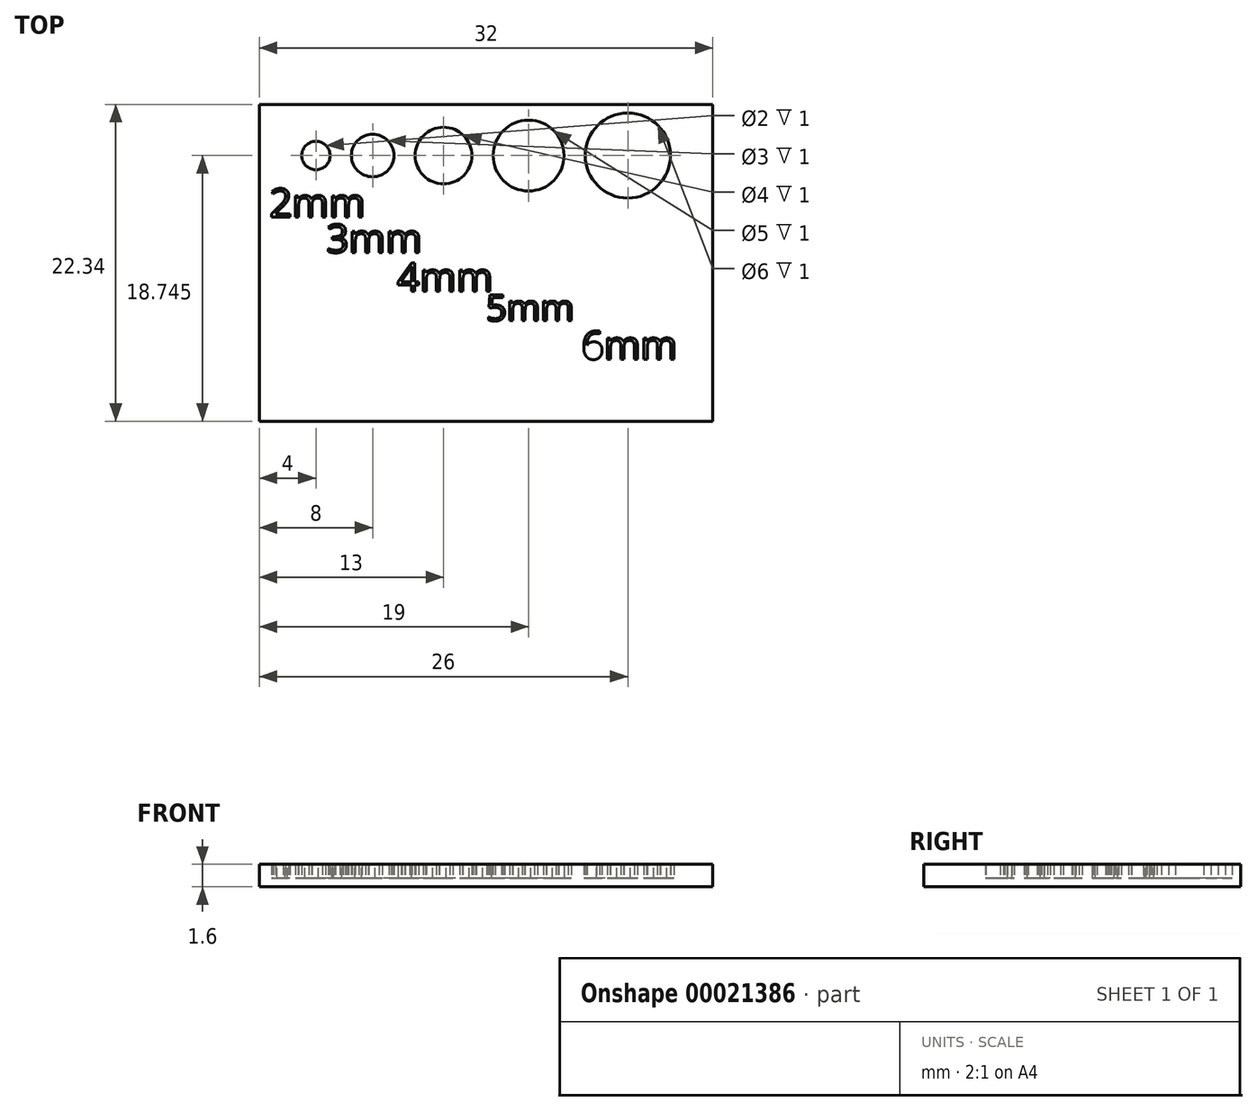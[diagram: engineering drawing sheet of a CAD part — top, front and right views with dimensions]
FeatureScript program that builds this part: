
annotation { "Feature Type Name" : "Feature", "Feature Type Description" : "" }
export const myFeature = defineFeature(function(context is Context, id is Id, definition is map)
    precondition{}
    {
        {
            var Q0;
            Q0=qCreatedBy(makeId("Top.planeOp"),FACE);
            var sketch = newSketch(context, id + "F0", { "sketchPlane" : qUnion([Q0])});
            skLineSegment(sketch, "E0.rect.bottom", {"start": v(-16, 11.17) * mm, "end": v(16, 11.17) * mm});
            skLineSegment(sketch, "E0.rect.top", {"start": v(-16, -11.17) * mm, "end": v(16, -11.17) * mm});
            skLineSegment(sketch, "E0.rect.left", {"start": v(-16, 11.17) * mm, "end": v(-16, -11.17) * mm});
            skLineSegment(sketch, "E0.rect.right", {"start": v(16, 11.17) * mm, "end": v(16, -11.17) * mm});
            skPoint(sketch, "E0.rect.middle", {"position": v(0, 0) * mm});
            skCircle(sketch, "E1", {"center": v(-12, 7.58) * mm, "radius": 1 * mm});
            skCircle(sketch, "E2", {"center": v(-8, 7.58) * mm, "radius": 1.5 * mm});
            skCircle(sketch, "E3", {"center": v(-3, 7.58) * mm, "radius": 2 * mm});
            skCircle(sketch, "E4", {"center": v(3, 7.58) * mm, "radius": 2.5 * mm});
            skCircle(sketch, "E5", {"center": v(10, 7.58) * mm, "radius": 3 * mm});
            skText(sketch, "E6", { "text": "2mm", "fontName": "OpenSans-Regular.ttf"});
            skText(sketch, "E7", { "text": "3mm", "fontName": "OpenSans-Regular.ttf"});
            skText(sketch, "E8", { "text": "4mm", "fontName": "OpenSans-Regular.ttf"});
            skText(sketch, "E9", { "text": "5mm", "fontName": "OpenSans-Regular.ttf"});
            skText(sketch, "E10", { "text": "6mm", "fontName": "OpenSans-Regular.ttf"});
            const initialGuessF0  = {"E6": [-0.01527, 0.00325, 1, 0, 0.002], "E7": [-0.01127, 0.00073, 1, 0, 0.002], "E8": [-0.00627, -0.002, 1, 0, 0.002], "E9": [0, -0.00408, 1, 0, 0.00184], "E10": [0.00673, -0.0068, 1, 0, 0.002]};
            skSetInitialGuess(sketch, initialGuessF0);
            skSolve(sketch);
        }
        {
            var Q0;
            Q0 = qSketchRegion(id + "F0", true);
            var Q1;
            Q1=makeQuery(id+"F0.imprint","IMPRINT",FACE,{"disambiguationData":[TD([[makeQuery(id+"F0.imprint","IMPRINT",EDGE,{"derivedFrom":sQuery(id+"F0.wireOp",EDGE,"E8.sketch_text.stroke-11")}),1.0]])]});
            extrude(context, id + "F1", {"entities" : qUnion([Q0, Q1]), "depth" : 1 * mm});
        }
        {
            var Q0;
            Q0=makeQuery(id+"F1.opExtrude","CAP_FACE",FACE,{"disambiguationData":[OSD([sQuery(id+"F0.wireOp",EDGE,"E0.rect.bottom"),sQuery(id+"F0.wireOp",EDGE,"E0.rect.top"),sQuery(id+"F0.wireOp",EDGE,"E0.rect.left"),sQuery(id+"F0.wireOp",EDGE,"E0.rect.right"),sQuery(id+"F0.wireOp",EDGE,"E1"),sQuery(id+"F0.wireOp",EDGE,"E2"),sQuery(id+"F0.wireOp",EDGE,"E3"),sQuery(id+"F0.wireOp",EDGE,"E4"),sQuery(id+"F0.wireOp",EDGE,"E5"),sQuery(id+"F0.wireOp",EDGE,"E6.sketch_text.stroke-0"),sQuery(id+"F0.wireOp",EDGE,"E6.sketch_text.stroke-1"),sQuery(id+"F0.wireOp",EDGE,"E6.sketch_text.stroke-2"),sQuery(id+"F0.wireOp",EDGE,"E6.sketch_text.stroke-3"),sQuery(id+"F0.wireOp",EDGE,"E6.sketch_text.stroke-4"),sQuery(id+"F0.wireOp",EDGE,"E6.sketch_text.stroke-5"),sQuery(id+"F0.wireOp",EDGE,"E6.sketch_text.stroke-6"),sQuery(id+"F0.wireOp",EDGE,"E6.sketch_text.stroke-7"),sQuery(id+"F0.wireOp",EDGE,"E6.sketch_text.stroke-8"),sQuery(id+"F0.wireOp",EDGE,"E6.sketch_text.stroke-9"),sQuery(id+"F0.wireOp",EDGE,"E6.sketch_text.stroke-10"),sQuery(id+"F0.wireOp",EDGE,"E6.sketch_text.stroke-11"),sQuery(id+"F0.wireOp",EDGE,"E6.sketch_text.stroke-12"),sQuery(id+"F0.wireOp",EDGE,"E6.sketch_text.stroke-13"),sQuery(id+"F0.wireOp",EDGE,"E6.sketch_text.stroke-14"),sQuery(id+"F0.wireOp",EDGE,"E6.sketch_text.stroke-15"),sQuery(id+"F0.wireOp",EDGE,"E6.sketch_text.stroke-16"),sQuery(id+"F0.wireOp",EDGE,"E6.sketch_text.stroke-17"),sQuery(id+"F0.wireOp",EDGE,"E6.sketch_text.stroke-18"),sQuery(id+"F0.wireOp",EDGE,"E6.sketch_text.stroke-19"),sQuery(id+"F0.wireOp",EDGE,"E6.sketch_text.stroke-20"),sQuery(id+"F0.wireOp",EDGE,"E6.sketch_text.stroke-21"),sQuery(id+"F0.wireOp",EDGE,"E6.sketch_text.stroke-22"),sQuery(id+"F0.wireOp",EDGE,"E6.sketch_text.stroke-23"),sQuery(id+"F0.wireOp",EDGE,"E6.sketch_text.stroke-24"),sQuery(id+"F0.wireOp",EDGE,"E6.sketch_text.stroke-25"),sQuery(id+"F0.wireOp",EDGE,"E6.sketch_text.stroke-26"),sQuery(id+"F0.wireOp",EDGE,"E6.sketch_text.stroke-27"),sQuery(id+"F0.wireOp",EDGE,"E6.sketch_text.stroke-28"),sQuery(id+"F0.wireOp",EDGE,"E6.sketch_text.stroke-29"),sQuery(id+"F0.wireOp",EDGE,"E6.sketch_text.stroke-30"),sQuery(id+"F0.wireOp",EDGE,"E6.sketch_text.stroke-31"),sQuery(id+"F0.wireOp",EDGE,"E6.sketch_text.stroke-32"),sQuery(id+"F0.wireOp",EDGE,"E6.sketch_text.stroke-33"),sQuery(id+"F0.wireOp",EDGE,"E6.sketch_text.stroke-34"),sQuery(id+"F0.wireOp",EDGE,"E6.sketch_text.stroke-35"),sQuery(id+"F0.wireOp",EDGE,"E6.sketch_text.stroke-36"),sQuery(id+"F0.wireOp",EDGE,"E6.sketch_text.stroke-37"),sQuery(id+"F0.wireOp",EDGE,"E6.sketch_text.stroke-38"),sQuery(id+"F0.wireOp",EDGE,"E6.sketch_text.stroke-39"),sQuery(id+"F0.wireOp",EDGE,"E6.sketch_text.stroke-40"),sQuery(id+"F0.wireOp",EDGE,"E6.sketch_text.stroke-41"),sQuery(id+"F0.wireOp",EDGE,"E6.sketch_text.stroke-42"),sQuery(id+"F0.wireOp",EDGE,"E6.sketch_text.stroke-43"),sQuery(id+"F0.wireOp",EDGE,"E6.sketch_text.stroke-44"),sQuery(id+"F0.wireOp",EDGE,"E6.sketch_text.stroke-45"),sQuery(id+"F0.wireOp",EDGE,"E6.sketch_text.stroke-46"),sQuery(id+"F0.wireOp",EDGE,"E6.sketch_text.stroke-47"),sQuery(id+"F0.wireOp",EDGE,"E6.sketch_text.stroke-48"),sQuery(id+"F0.wireOp",EDGE,"E6.sketch_text.stroke-49"),sQuery(id+"F0.wireOp",EDGE,"E6.sketch_text.stroke-50"),sQuery(id+"F0.wireOp",EDGE,"E6.sketch_text.stroke-51"),sQuery(id+"F0.wireOp",EDGE,"E6.sketch_text.stroke-52"),sQuery(id+"F0.wireOp",EDGE,"E6.sketch_text.stroke-53"),sQuery(id+"F0.wireOp",EDGE,"E6.sketch_text.stroke-54"),sQuery(id+"F0.wireOp",EDGE,"E6.sketch_text.stroke-55"),sQuery(id+"F0.wireOp",EDGE,"E6.sketch_text.stroke-56"),sQuery(id+"F0.wireOp",EDGE,"E6.sketch_text.stroke-57"),sQuery(id+"F0.wireOp",EDGE,"E6.sketch_text.stroke-58"),sQuery(id+"F0.wireOp",EDGE,"E6.sketch_text.stroke-59"),sQuery(id+"F0.wireOp",EDGE,"E6.sketch_text.stroke-60"),sQuery(id+"F0.wireOp",EDGE,"E6.sketch_text.stroke-61"),sQuery(id+"F0.wireOp",EDGE,"E6.sketch_text.stroke-62"),sQuery(id+"F0.wireOp",EDGE,"E6.sketch_text.stroke-63"),sQuery(id+"F0.wireOp",EDGE,"E6.sketch_text.stroke-64"),sQuery(id+"F0.wireOp",EDGE,"E6.sketch_text.stroke-65"),sQuery(id+"F0.wireOp",EDGE,"E6.sketch_text.stroke-66"),sQuery(id+"F0.wireOp",EDGE,"E6.sketch_text.stroke-67"),sQuery(id+"F0.wireOp",EDGE,"E6.sketch_text.stroke-68"),sQuery(id+"F0.wireOp",EDGE,"E6.sketch_text.stroke-69"),sQuery(id+"F0.wireOp",EDGE,"E6.sketch_text.stroke-70"),sQuery(id+"F0.wireOp",EDGE,"E6.sketch_text.stroke-71"),sQuery(id+"F0.wireOp",EDGE,"E6.sketch_text.stroke-72"),sQuery(id+"F0.wireOp",EDGE,"E6.sketch_text.stroke-73"),sQuery(id+"F0.wireOp",EDGE,"E6.sketch_text.stroke-74"),sQuery(id+"F0.wireOp",EDGE,"E6.sketch_text.stroke-75"),sQuery(id+"F0.wireOp",EDGE,"E7.sketch_text.stroke-0"),sQuery(id+"F0.wireOp",EDGE,"E7.sketch_text.stroke-1"),sQuery(id+"F0.wireOp",EDGE,"E7.sketch_text.stroke-2"),sQuery(id+"F0.wireOp",EDGE,"E7.sketch_text.stroke-3"),sQuery(id+"F0.wireOp",EDGE,"E7.sketch_text.stroke-4"),sQuery(id+"F0.wireOp",EDGE,"E7.sketch_text.stroke-5"),sQuery(id+"F0.wireOp",EDGE,"E7.sketch_text.stroke-6"),sQuery(id+"F0.wireOp",EDGE,"E7.sketch_text.stroke-7"),sQuery(id+"F0.wireOp",EDGE,"E7.sketch_text.stroke-8"),sQuery(id+"F0.wireOp",EDGE,"E7.sketch_text.stroke-9"),sQuery(id+"F0.wireOp",EDGE,"E7.sketch_text.stroke-10"),sQuery(id+"F0.wireOp",EDGE,"E7.sketch_text.stroke-11"),sQuery(id+"F0.wireOp",EDGE,"E7.sketch_text.stroke-12"),sQuery(id+"F0.wireOp",EDGE,"E7.sketch_text.stroke-13"),sQuery(id+"F0.wireOp",EDGE,"E7.sketch_text.stroke-14"),sQuery(id+"F0.wireOp",EDGE,"E7.sketch_text.stroke-15"),sQuery(id+"F0.wireOp",EDGE,"E7.sketch_text.stroke-16"),sQuery(id+"F0.wireOp",EDGE,"E7.sketch_text.stroke-17"),sQuery(id+"F0.wireOp",EDGE,"E7.sketch_text.stroke-18"),sQuery(id+"F0.wireOp",EDGE,"E7.sketch_text.stroke-19"),sQuery(id+"F0.wireOp",EDGE,"E7.sketch_text.stroke-20"),sQuery(id+"F0.wireOp",EDGE,"E7.sketch_text.stroke-21"),sQuery(id+"F0.wireOp",EDGE,"E7.sketch_text.stroke-22"),sQuery(id+"F0.wireOp",EDGE,"E7.sketch_text.stroke-23"),sQuery(id+"F0.wireOp",EDGE,"E7.sketch_text.stroke-24"),sQuery(id+"F0.wireOp",EDGE,"E7.sketch_text.stroke-25"),sQuery(id+"F0.wireOp",EDGE,"E7.sketch_text.stroke-26"),sQuery(id+"F0.wireOp",EDGE,"E7.sketch_text.stroke-27"),sQuery(id+"F0.wireOp",EDGE,"E7.sketch_text.stroke-28"),sQuery(id+"F0.wireOp",EDGE,"E7.sketch_text.stroke-29"),sQuery(id+"F0.wireOp",EDGE,"E7.sketch_text.stroke-30"),sQuery(id+"F0.wireOp",EDGE,"E7.sketch_text.stroke-31"),sQuery(id+"F0.wireOp",EDGE,"E7.sketch_text.stroke-32"),sQuery(id+"F0.wireOp",EDGE,"E7.sketch_text.stroke-33"),sQuery(id+"F0.wireOp",EDGE,"E7.sketch_text.stroke-34"),sQuery(id+"F0.wireOp",EDGE,"E7.sketch_text.stroke-35"),sQuery(id+"F0.wireOp",EDGE,"E7.sketch_text.stroke-36"),sQuery(id+"F0.wireOp",EDGE,"E7.sketch_text.stroke-37"),sQuery(id+"F0.wireOp",EDGE,"E7.sketch_text.stroke-38"),sQuery(id+"F0.wireOp",EDGE,"E7.sketch_text.stroke-39"),sQuery(id+"F0.wireOp",EDGE,"E7.sketch_text.stroke-40"),sQuery(id+"F0.wireOp",EDGE,"E7.sketch_text.stroke-41"),sQuery(id+"F0.wireOp",EDGE,"E7.sketch_text.stroke-42"),sQuery(id+"F0.wireOp",EDGE,"E7.sketch_text.stroke-43"),sQuery(id+"F0.wireOp",EDGE,"E7.sketch_text.stroke-44"),sQuery(id+"F0.wireOp",EDGE,"E7.sketch_text.stroke-45"),sQuery(id+"F0.wireOp",EDGE,"E7.sketch_text.stroke-46"),sQuery(id+"F0.wireOp",EDGE,"E7.sketch_text.stroke-47"),sQuery(id+"F0.wireOp",EDGE,"E7.sketch_text.stroke-48"),sQuery(id+"F0.wireOp",EDGE,"E7.sketch_text.stroke-49"),sQuery(id+"F0.wireOp",EDGE,"E7.sketch_text.stroke-50"),sQuery(id+"F0.wireOp",EDGE,"E7.sketch_text.stroke-51"),sQuery(id+"F0.wireOp",EDGE,"E7.sketch_text.stroke-52"),sQuery(id+"F0.wireOp",EDGE,"E7.sketch_text.stroke-53"),sQuery(id+"F0.wireOp",EDGE,"E7.sketch_text.stroke-54"),sQuery(id+"F0.wireOp",EDGE,"E7.sketch_text.stroke-55"),sQuery(id+"F0.wireOp",EDGE,"E7.sketch_text.stroke-56"),sQuery(id+"F0.wireOp",EDGE,"E7.sketch_text.stroke-57"),sQuery(id+"F0.wireOp",EDGE,"E7.sketch_text.stroke-58"),sQuery(id+"F0.wireOp",EDGE,"E7.sketch_text.stroke-59"),sQuery(id+"F0.wireOp",EDGE,"E7.sketch_text.stroke-60"),sQuery(id+"F0.wireOp",EDGE,"E7.sketch_text.stroke-61"),sQuery(id+"F0.wireOp",EDGE,"E7.sketch_text.stroke-62"),sQuery(id+"F0.wireOp",EDGE,"E7.sketch_text.stroke-63"),sQuery(id+"F0.wireOp",EDGE,"E7.sketch_text.stroke-64"),sQuery(id+"F0.wireOp",EDGE,"E7.sketch_text.stroke-65"),sQuery(id+"F0.wireOp",EDGE,"E7.sketch_text.stroke-66"),sQuery(id+"F0.wireOp",EDGE,"E7.sketch_text.stroke-67"),sQuery(id+"F0.wireOp",EDGE,"E7.sketch_text.stroke-68"),sQuery(id+"F0.wireOp",EDGE,"E7.sketch_text.stroke-69"),sQuery(id+"F0.wireOp",EDGE,"E7.sketch_text.stroke-70"),sQuery(id+"F0.wireOp",EDGE,"E7.sketch_text.stroke-71"),sQuery(id+"F0.wireOp",EDGE,"E7.sketch_text.stroke-72"),sQuery(id+"F0.wireOp",EDGE,"E7.sketch_text.stroke-73"),sQuery(id+"F0.wireOp",EDGE,"E7.sketch_text.stroke-74"),sQuery(id+"F0.wireOp",EDGE,"E7.sketch_text.stroke-75"),sQuery(id+"F0.wireOp",EDGE,"E7.sketch_text.stroke-76"),sQuery(id+"F0.wireOp",EDGE,"E7.sketch_text.stroke-77"),sQuery(id+"F0.wireOp",EDGE,"E7.sketch_text.stroke-78"),sQuery(id+"F0.wireOp",EDGE,"E7.sketch_text.stroke-79"),sQuery(id+"F0.wireOp",EDGE,"E7.sketch_text.stroke-80"),sQuery(id+"F0.wireOp",EDGE,"E7.sketch_text.stroke-81"),sQuery(id+"F0.wireOp",EDGE,"E7.sketch_text.stroke-82"),sQuery(id+"F0.wireOp",EDGE,"E7.sketch_text.stroke-83"),sQuery(id+"F0.wireOp",EDGE,"E8.sketch_text.stroke-0"),sQuery(id+"F0.wireOp",EDGE,"E8.sketch_text.stroke-1"),sQuery(id+"F0.wireOp",EDGE,"E8.sketch_text.stroke-2"),sQuery(id+"F0.wireOp",EDGE,"E8.sketch_text.stroke-3"),sQuery(id+"F0.wireOp",EDGE,"E8.sketch_text.stroke-4"),sQuery(id+"F0.wireOp",EDGE,"E8.sketch_text.stroke-5"),sQuery(id+"F0.wireOp",EDGE,"E8.sketch_text.stroke-6"),sQuery(id+"F0.wireOp",EDGE,"E8.sketch_text.stroke-7"),sQuery(id+"F0.wireOp",EDGE,"E8.sketch_text.stroke-8"),sQuery(id+"F0.wireOp",EDGE,"E8.sketch_text.stroke-9"),sQuery(id+"F0.wireOp",EDGE,"E8.sketch_text.stroke-10"),sQuery(id+"F0.wireOp",EDGE,"E8.sketch_text.stroke-17"),sQuery(id+"F0.wireOp",EDGE,"E8.sketch_text.stroke-18"),sQuery(id+"F0.wireOp",EDGE,"E8.sketch_text.stroke-19"),sQuery(id+"F0.wireOp",EDGE,"E8.sketch_text.stroke-20"),sQuery(id+"F0.wireOp",EDGE,"E8.sketch_text.stroke-21"),sQuery(id+"F0.wireOp",EDGE,"E8.sketch_text.stroke-22"),sQuery(id+"F0.wireOp",EDGE,"E8.sketch_text.stroke-23"),sQuery(id+"F0.wireOp",EDGE,"E8.sketch_text.stroke-24"),sQuery(id+"F0.wireOp",EDGE,"E8.sketch_text.stroke-25"),sQuery(id+"F0.wireOp",EDGE,"E8.sketch_text.stroke-26"),sQuery(id+"F0.wireOp",EDGE,"E8.sketch_text.stroke-27"),sQuery(id+"F0.wireOp",EDGE,"E8.sketch_text.stroke-28"),sQuery(id+"F0.wireOp",EDGE,"E8.sketch_text.stroke-29"),sQuery(id+"F0.wireOp",EDGE,"E8.sketch_text.stroke-30"),sQuery(id+"F0.wireOp",EDGE,"E8.sketch_text.stroke-31"),sQuery(id+"F0.wireOp",EDGE,"E8.sketch_text.stroke-32"),sQuery(id+"F0.wireOp",EDGE,"E8.sketch_text.stroke-33"),sQuery(id+"F0.wireOp",EDGE,"E8.sketch_text.stroke-34"),sQuery(id+"F0.wireOp",EDGE,"E8.sketch_text.stroke-35"),sQuery(id+"F0.wireOp",EDGE,"E8.sketch_text.stroke-36"),sQuery(id+"F0.wireOp",EDGE,"E8.sketch_text.stroke-37"),sQuery(id+"F0.wireOp",EDGE,"E8.sketch_text.stroke-38"),sQuery(id+"F0.wireOp",EDGE,"E8.sketch_text.stroke-39"),sQuery(id+"F0.wireOp",EDGE,"E8.sketch_text.stroke-40"),sQuery(id+"F0.wireOp",EDGE,"E8.sketch_text.stroke-41"),sQuery(id+"F0.wireOp",EDGE,"E8.sketch_text.stroke-42"),sQuery(id+"F0.wireOp",EDGE,"E8.sketch_text.stroke-43"),sQuery(id+"F0.wireOp",EDGE,"E8.sketch_text.stroke-44"),sQuery(id+"F0.wireOp",EDGE,"E8.sketch_text.stroke-45"),sQuery(id+"F0.wireOp",EDGE,"E8.sketch_text.stroke-46"),sQuery(id+"F0.wireOp",EDGE,"E8.sketch_text.stroke-47"),sQuery(id+"F0.wireOp",EDGE,"E8.sketch_text.stroke-48"),sQuery(id+"F0.wireOp",EDGE,"E8.sketch_text.stroke-49"),sQuery(id+"F0.wireOp",EDGE,"E8.sketch_text.stroke-50"),sQuery(id+"F0.wireOp",EDGE,"E8.sketch_text.stroke-51"),sQuery(id+"F0.wireOp",EDGE,"E8.sketch_text.stroke-52"),sQuery(id+"F0.wireOp",EDGE,"E8.sketch_text.stroke-53"),sQuery(id+"F0.wireOp",EDGE,"E8.sketch_text.stroke-54"),sQuery(id+"F0.wireOp",EDGE,"E8.sketch_text.stroke-55"),sQuery(id+"F0.wireOp",EDGE,"E8.sketch_text.stroke-56"),sQuery(id+"F0.wireOp",EDGE,"E8.sketch_text.stroke-57"),sQuery(id+"F0.wireOp",EDGE,"E8.sketch_text.stroke-58"),sQuery(id+"F0.wireOp",EDGE,"E8.sketch_text.stroke-59"),sQuery(id+"F0.wireOp",EDGE,"E8.sketch_text.stroke-60"),sQuery(id+"F0.wireOp",EDGE,"E8.sketch_text.stroke-61"),sQuery(id+"F0.wireOp",EDGE,"E8.sketch_text.stroke-62"),sQuery(id+"F0.wireOp",EDGE,"E8.sketch_text.stroke-63"),sQuery(id+"F0.wireOp",EDGE,"E8.sketch_text.stroke-64"),sQuery(id+"F0.wireOp",EDGE,"E8.sketch_text.stroke-65"),sQuery(id+"F0.wireOp",EDGE,"E8.sketch_text.stroke-66"),sQuery(id+"F0.wireOp",EDGE,"E8.sketch_text.stroke-67"),sQuery(id+"F0.wireOp",EDGE,"E8.sketch_text.stroke-68"),sQuery(id+"F0.wireOp",EDGE,"E8.sketch_text.stroke-69"),sQuery(id+"F0.wireOp",EDGE,"E8.sketch_text.stroke-70"),sQuery(id+"F0.wireOp",EDGE,"E8.sketch_text.stroke-71"),sQuery(id+"F0.wireOp",EDGE,"E8.sketch_text.stroke-72"),sQuery(id+"F0.wireOp",EDGE,"E9.sketch_text.stroke-0"),sQuery(id+"F0.wireOp",EDGE,"E9.sketch_text.stroke-1"),sQuery(id+"F0.wireOp",EDGE,"E9.sketch_text.stroke-2"),sQuery(id+"F0.wireOp",EDGE,"E9.sketch_text.stroke-3"),sQuery(id+"F0.wireOp",EDGE,"E9.sketch_text.stroke-4"),sQuery(id+"F0.wireOp",EDGE,"E9.sketch_text.stroke-5"),sQuery(id+"F0.wireOp",EDGE,"E9.sketch_text.stroke-6"),sQuery(id+"F0.wireOp",EDGE,"E9.sketch_text.stroke-7"),sQuery(id+"F0.wireOp",EDGE,"E9.sketch_text.stroke-8"),sQuery(id+"F0.wireOp",EDGE,"E9.sketch_text.stroke-9"),sQuery(id+"F0.wireOp",EDGE,"E9.sketch_text.stroke-10"),sQuery(id+"F0.wireOp",EDGE,"E9.sketch_text.stroke-11"),sQuery(id+"F0.wireOp",EDGE,"E9.sketch_text.stroke-12"),sQuery(id+"F0.wireOp",EDGE,"E9.sketch_text.stroke-13"),sQuery(id+"F0.wireOp",EDGE,"E9.sketch_text.stroke-14"),sQuery(id+"F0.wireOp",EDGE,"E9.sketch_text.stroke-15"),sQuery(id+"F0.wireOp",EDGE,"E9.sketch_text.stroke-16"),sQuery(id+"F0.wireOp",EDGE,"E9.sketch_text.stroke-17"),sQuery(id+"F0.wireOp",EDGE,"E9.sketch_text.stroke-18"),sQuery(id+"F0.wireOp",EDGE,"E9.sketch_text.stroke-19"),sQuery(id+"F0.wireOp",EDGE,"E9.sketch_text.stroke-20"),sQuery(id+"F0.wireOp",EDGE,"E9.sketch_text.stroke-21"),sQuery(id+"F0.wireOp",EDGE,"E9.sketch_text.stroke-22"),sQuery(id+"F0.wireOp",EDGE,"E9.sketch_text.stroke-23"),sQuery(id+"F0.wireOp",EDGE,"E9.sketch_text.stroke-24"),sQuery(id+"F0.wireOp",EDGE,"E9.sketch_text.stroke-25"),sQuery(id+"F0.wireOp",EDGE,"E9.sketch_text.stroke-26"),sQuery(id+"F0.wireOp",EDGE,"E9.sketch_text.stroke-27"),sQuery(id+"F0.wireOp",EDGE,"E9.sketch_text.stroke-28"),sQuery(id+"F0.wireOp",EDGE,"E9.sketch_text.stroke-29"),sQuery(id+"F0.wireOp",EDGE,"E9.sketch_text.stroke-30"),sQuery(id+"F0.wireOp",EDGE,"E9.sketch_text.stroke-31"),sQuery(id+"F0.wireOp",EDGE,"E9.sketch_text.stroke-32"),sQuery(id+"F0.wireOp",EDGE,"E9.sketch_text.stroke-33"),sQuery(id+"F0.wireOp",EDGE,"E9.sketch_text.stroke-34"),sQuery(id+"F0.wireOp",EDGE,"E9.sketch_text.stroke-35"),sQuery(id+"F0.wireOp",EDGE,"E9.sketch_text.stroke-36"),sQuery(id+"F0.wireOp",EDGE,"E9.sketch_text.stroke-37"),sQuery(id+"F0.wireOp",EDGE,"E9.sketch_text.stroke-38"),sQuery(id+"F0.wireOp",EDGE,"E9.sketch_text.stroke-39"),sQuery(id+"F0.wireOp",EDGE,"E9.sketch_text.stroke-40"),sQuery(id+"F0.wireOp",EDGE,"E9.sketch_text.stroke-41"),sQuery(id+"F0.wireOp",EDGE,"E9.sketch_text.stroke-42"),sQuery(id+"F0.wireOp",EDGE,"E9.sketch_text.stroke-43"),sQuery(id+"F0.wireOp",EDGE,"E9.sketch_text.stroke-44"),sQuery(id+"F0.wireOp",EDGE,"E9.sketch_text.stroke-45"),sQuery(id+"F0.wireOp",EDGE,"E9.sketch_text.stroke-46"),sQuery(id+"F0.wireOp",EDGE,"E9.sketch_text.stroke-47"),sQuery(id+"F0.wireOp",EDGE,"E9.sketch_text.stroke-48"),sQuery(id+"F0.wireOp",EDGE,"E9.sketch_text.stroke-49"),sQuery(id+"F0.wireOp",EDGE,"E9.sketch_text.stroke-50"),sQuery(id+"F0.wireOp",EDGE,"E9.sketch_text.stroke-51"),sQuery(id+"F0.wireOp",EDGE,"E9.sketch_text.stroke-52"),sQuery(id+"F0.wireOp",EDGE,"E9.sketch_text.stroke-53"),sQuery(id+"F0.wireOp",EDGE,"E9.sketch_text.stroke-54"),sQuery(id+"F0.wireOp",EDGE,"E9.sketch_text.stroke-55"),sQuery(id+"F0.wireOp",EDGE,"E9.sketch_text.stroke-56"),sQuery(id+"F0.wireOp",EDGE,"E9.sketch_text.stroke-57"),sQuery(id+"F0.wireOp",EDGE,"E9.sketch_text.stroke-58"),sQuery(id+"F0.wireOp",EDGE,"E9.sketch_text.stroke-59"),sQuery(id+"F0.wireOp",EDGE,"E9.sketch_text.stroke-60"),sQuery(id+"F0.wireOp",EDGE,"E9.sketch_text.stroke-61"),sQuery(id+"F0.wireOp",EDGE,"E9.sketch_text.stroke-62"),sQuery(id+"F0.wireOp",EDGE,"E9.sketch_text.stroke-63"),sQuery(id+"F0.wireOp",EDGE,"E9.sketch_text.stroke-64"),sQuery(id+"F0.wireOp",EDGE,"E9.sketch_text.stroke-65"),sQuery(id+"F0.wireOp",EDGE,"E9.sketch_text.stroke-66"),sQuery(id+"F0.wireOp",EDGE,"E9.sketch_text.stroke-67"),sQuery(id+"F0.wireOp",EDGE,"E9.sketch_text.stroke-68"),sQuery(id+"F0.wireOp",EDGE,"E9.sketch_text.stroke-69"),sQuery(id+"F0.wireOp",EDGE,"E9.sketch_text.stroke-70"),sQuery(id+"F0.wireOp",EDGE,"E9.sketch_text.stroke-71"),sQuery(id+"F0.wireOp",EDGE,"E9.sketch_text.stroke-72"),sQuery(id+"F0.wireOp",EDGE,"E9.sketch_text.stroke-73"),sQuery(id+"F0.wireOp",EDGE,"E9.sketch_text.stroke-74"),sQuery(id+"F0.wireOp",EDGE,"E10.sketch_text.stroke-0"),sQuery(id+"F0.wireOp",EDGE,"E10.sketch_text.stroke-1"),sQuery(id+"F0.wireOp",EDGE,"E10.sketch_text.stroke-2"),sQuery(id+"F0.wireOp",EDGE,"E10.sketch_text.stroke-3"),sQuery(id+"F0.wireOp",EDGE,"E10.sketch_text.stroke-4"),sQuery(id+"F0.wireOp",EDGE,"E10.sketch_text.stroke-5"),sQuery(id+"F0.wireOp",EDGE,"E10.sketch_text.stroke-6"),sQuery(id+"F0.wireOp",EDGE,"E10.sketch_text.stroke-7"),sQuery(id+"F0.wireOp",EDGE,"E10.sketch_text.stroke-8"),sQuery(id+"F0.wireOp",EDGE,"E10.sketch_text.stroke-9"),sQuery(id+"F0.wireOp",EDGE,"E10.sketch_text.stroke-10"),sQuery(id+"F0.wireOp",EDGE,"E10.sketch_text.stroke-11"),sQuery(id+"F0.wireOp",EDGE,"E10.sketch_text.stroke-12"),sQuery(id+"F0.wireOp",EDGE,"E10.sketch_text.stroke-13"),sQuery(id+"F0.wireOp",EDGE,"E10.sketch_text.stroke-14"),sQuery(id+"F0.wireOp",EDGE,"E10.sketch_text.stroke-25"),sQuery(id+"F0.wireOp",EDGE,"E10.sketch_text.stroke-26"),sQuery(id+"F0.wireOp",EDGE,"E10.sketch_text.stroke-27"),sQuery(id+"F0.wireOp",EDGE,"E10.sketch_text.stroke-28"),sQuery(id+"F0.wireOp",EDGE,"E10.sketch_text.stroke-29"),sQuery(id+"F0.wireOp",EDGE,"E10.sketch_text.stroke-30"),sQuery(id+"F0.wireOp",EDGE,"E10.sketch_text.stroke-31"),sQuery(id+"F0.wireOp",EDGE,"E10.sketch_text.stroke-32"),sQuery(id+"F0.wireOp",EDGE,"E10.sketch_text.stroke-33"),sQuery(id+"F0.wireOp",EDGE,"E10.sketch_text.stroke-34"),sQuery(id+"F0.wireOp",EDGE,"E10.sketch_text.stroke-35"),sQuery(id+"F0.wireOp",EDGE,"E10.sketch_text.stroke-36"),sQuery(id+"F0.wireOp",EDGE,"E10.sketch_text.stroke-37"),sQuery(id+"F0.wireOp",EDGE,"E10.sketch_text.stroke-38"),sQuery(id+"F0.wireOp",EDGE,"E10.sketch_text.stroke-39"),sQuery(id+"F0.wireOp",EDGE,"E10.sketch_text.stroke-40"),sQuery(id+"F0.wireOp",EDGE,"E10.sketch_text.stroke-41"),sQuery(id+"F0.wireOp",EDGE,"E10.sketch_text.stroke-42"),sQuery(id+"F0.wireOp",EDGE,"E10.sketch_text.stroke-43"),sQuery(id+"F0.wireOp",EDGE,"E10.sketch_text.stroke-44"),sQuery(id+"F0.wireOp",EDGE,"E10.sketch_text.stroke-45"),sQuery(id+"F0.wireOp",EDGE,"E10.sketch_text.stroke-46"),sQuery(id+"F0.wireOp",EDGE,"E10.sketch_text.stroke-47"),sQuery(id+"F0.wireOp",EDGE,"E10.sketch_text.stroke-48"),sQuery(id+"F0.wireOp",EDGE,"E10.sketch_text.stroke-49"),sQuery(id+"F0.wireOp",EDGE,"E10.sketch_text.stroke-50"),sQuery(id+"F0.wireOp",EDGE,"E10.sketch_text.stroke-51"),sQuery(id+"F0.wireOp",EDGE,"E10.sketch_text.stroke-52"),sQuery(id+"F0.wireOp",EDGE,"E10.sketch_text.stroke-53"),sQuery(id+"F0.wireOp",EDGE,"E10.sketch_text.stroke-54"),sQuery(id+"F0.wireOp",EDGE,"E10.sketch_text.stroke-55"),sQuery(id+"F0.wireOp",EDGE,"E10.sketch_text.stroke-56"),sQuery(id+"F0.wireOp",EDGE,"E10.sketch_text.stroke-57"),sQuery(id+"F0.wireOp",EDGE,"E10.sketch_text.stroke-58"),sQuery(id+"F0.wireOp",EDGE,"E10.sketch_text.stroke-59"),sQuery(id+"F0.wireOp",EDGE,"E10.sketch_text.stroke-60"),sQuery(id+"F0.wireOp",EDGE,"E10.sketch_text.stroke-61"),sQuery(id+"F0.wireOp",EDGE,"E10.sketch_text.stroke-62"),sQuery(id+"F0.wireOp",EDGE,"E10.sketch_text.stroke-63"),sQuery(id+"F0.wireOp",EDGE,"E10.sketch_text.stroke-64"),sQuery(id+"F0.wireOp",EDGE,"E10.sketch_text.stroke-65"),sQuery(id+"F0.wireOp",EDGE,"E10.sketch_text.stroke-66"),sQuery(id+"F0.wireOp",EDGE,"E10.sketch_text.stroke-67"),sQuery(id+"F0.wireOp",EDGE,"E10.sketch_text.stroke-68"),sQuery(id+"F0.wireOp",EDGE,"E10.sketch_text.stroke-69"),sQuery(id+"F0.wireOp",EDGE,"E10.sketch_text.stroke-70"),sQuery(id+"F0.wireOp",EDGE,"E10.sketch_text.stroke-71"),sQuery(id+"F0.wireOp",EDGE,"E10.sketch_text.stroke-72"),sQuery(id+"F0.wireOp",EDGE,"E10.sketch_text.stroke-73"),sQuery(id+"F0.wireOp",EDGE,"E10.sketch_text.stroke-74"),sQuery(id+"F0.wireOp",EDGE,"E10.sketch_text.stroke-75"),sQuery(id+"F0.wireOp",EDGE,"E10.sketch_text.stroke-76"),sQuery(id+"F0.wireOp",EDGE,"E10.sketch_text.stroke-77"),sQuery(id+"F0.wireOp",EDGE,"E10.sketch_text.stroke-78"),sQuery(id+"F0.wireOp",EDGE,"E10.sketch_text.stroke-79"),sQuery(id+"F0.wireOp",EDGE,"E10.sketch_text.stroke-80")])],"isStart":true});
            var sketch = newSketch(context, id + "F2", { "sketchPlane" : qUnion([Q0])});
            skLineSegment(sketch, "E11.0", {"start": v(-16, -11.17) * mm, "end": v(-16, 11.17) * mm});
            skLineSegment(sketch, "E12.0", {"start": v(-16, 11.17) * mm, "end": v(16, 11.17) * mm});
            skLineSegment(sketch, "E13.0", {"start": v(16, -11.17) * mm, "end": v(16, 11.17) * mm});
            skLineSegment(sketch, "E14.0", {"start": v(-16, -11.17) * mm, "end": v(16, -11.17) * mm});
            skSolve(sketch);
        }
        {
            var Q0;
            Q0 = qSketchRegion(id + "F2", true);
            extrude(context, id + "F3", {"entities" : qUnion([Q0]), "operationType" : NewBodyOperationType.ADD, "depth" : .6 * mm});
        }
    });
